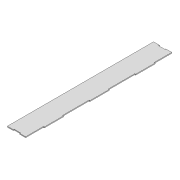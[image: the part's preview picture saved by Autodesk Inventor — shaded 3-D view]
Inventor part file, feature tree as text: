
AUTODESK INVENTOR PART (.ipt)
format: ipt  version: 2021 (Build 250183000, 183)  size: 130,048 bytes
history: native  units: mm
features: other x1, extrude x1, sketch x1
ambient origin geometry x8: Origin, YZ Plane, XZ Plane, XY Plane, X Axis, Y Axis, Z Axis, Center Point
bodies: Body1 (feature_tree)
feature tree (3):
  other  "Твердое тело1"
  extrude  "Выдавливание1"  Depth=681.0mm
  sketch  "Эскиз1"
